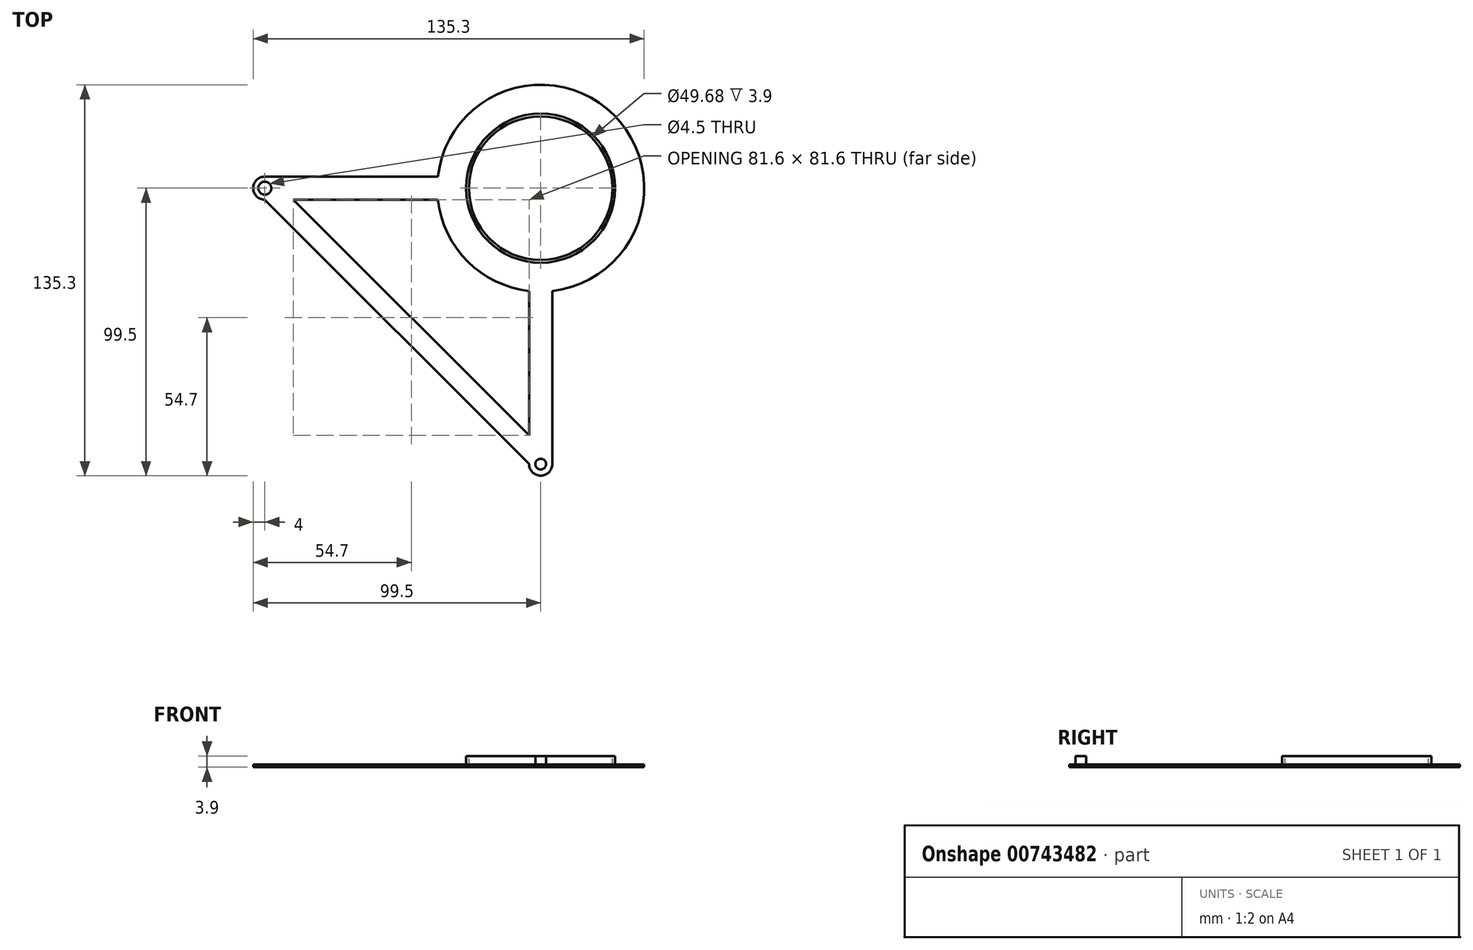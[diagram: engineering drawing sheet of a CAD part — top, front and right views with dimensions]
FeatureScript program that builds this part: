
annotation { "Feature Type Name" : "Feature", "Feature Type Description" : "" }
export const myFeature = defineFeature(function(context is Context, id is Id, definition is map)
    precondition{}
    {
        {
            var Q0;
            Q0=qCreatedBy(makeId("Top.planeOp"),FACE);
            var sketch = newSketch(context, id + "F0", { "sketchPlane" : qUnion([Q0])});
            skCircle(sketch, "E0", {"center": v(-95.5, 0) * mm, "radius": 2.25 * mm});
            skCircle(sketch, "E1", {"center": v(0, -95.5) * mm, "radius": 1.85 * mm});
            skCircle(sketch, "E2", {"center": v(0, 0) * mm, "radius": 24.84 * mm});
            skCircle(sketch, "E3", {"center": v(0, 0) * mm, "radius": 25.8 * mm});
            skCircle(sketch, "E4", {"center": v(0, 0) * mm, "radius": 35.8 * mm});
            skLineSegment(sketch, "E5.bottom", {"start": v(0, 4) * mm, "end": v(-95.5, 4) * mm});
            skLineSegment(sketch, "E5.top", {"start": v(0, -4) * mm, "end": v(-95.5, -4) * mm});
            skLineSegment(sketch, "E5.left", {"start": v(0, 4) * mm, "end": v(0, -4) * mm});
            skLineSegment(sketch, "E5.right", {"start": v(-95.5, 4) * mm, "end": v(-95.5, -4) * mm});
            skLineSegment(sketch, "E6.bottom", {"start": v(-4, 0) * mm, "end": v(4, 0) * mm});
            skLineSegment(sketch, "E6.top", {"start": v(-4, -95.5) * mm, "end": v(4, -95.5) * mm});
            skLineSegment(sketch, "E6.left", {"start": v(-4, 0) * mm, "end": v(-4, -95.5) * mm});
            skLineSegment(sketch, "E6.right", {"start": v(4, 0) * mm, "end": v(4, -95.5) * mm});
            skCircle(sketch, "E7", {"center": v(-95.5, 0) * mm, "radius": 4 * mm});
            skCircle(sketch, "E8", {"center": v(0, -95.5) * mm, "radius": 4 * mm});
            skLineSegment(sketch, "E9", {"start": v(-95.5, -4) * mm, "end": v(-4, -95.5) * mm});
            skLineSegment(sketch, "E10", {"start": v(-85.6, -4) * mm, "end": v(-4, -85.6) * mm});
            skSolve(sketch);
        }
        {
            var Q0;
            {var subQ5=sQuery(id+"F0.wireOp",EDGE,"E5.bottom");var subQ7=sQuery(id+"F0.wireOp",EDGE,"E4");var subQ9=makeQuery(id+"F0.imprint","INTERSECT",VERTEX,{"derivedFrom":[subQ7,subQ5]});Q0=makeQuery(id+"F0.imprint","IMPRINT",FACE,{"disambiguationData":[TD([[makeQuery(id+"F0.imprint","IMPRINT",EDGE,{"disambiguationData":[TD([[subQ9,-1.0]])],"derivedFrom":subQ7}),-1.0]])]});}
            var Q1;
            {var subQ0=sQuery(id+"F0.wireOp",EDGE,"E5.right");var subQ1=sQuery(id+"F0.wireOp",EDGE,"E0");var subQ2=makeQuery(id+"F0.imprint","INTERSECT",VERTEX,{"disambiguationData":[OD(0.0)],"derivedFrom":[subQ1,subQ0]});Q1=makeQuery(id+"F0.imprint","IMPRINT",FACE,{"disambiguationData":[TD([[makeQuery(id+"F0.imprint","IMPRINT",EDGE,{"disambiguationData":[TD([[subQ2,1.0]])],"derivedFrom":subQ1}),-1.0]])]});}
            var Q2;
            {var subQ0=sQuery(id+"F0.wireOp",EDGE,"E5.right");var subQ1=sQuery(id+"F0.wireOp",EDGE,"E0");var subQ2=makeQuery(id+"F0.imprint","INTERSECT",VERTEX,{"disambiguationData":[OD(0.0)],"derivedFrom":[subQ1,subQ0]});Q2=makeQuery(id+"F0.imprint","IMPRINT",FACE,{"disambiguationData":[TD([[makeQuery(id+"F0.imprint","IMPRINT",EDGE,{"disambiguationData":[TD([[subQ2,-1.0]])],"derivedFrom":subQ1}),-1.0]])]});}
            var Q3;
            {var subQ0=sQuery(id+"F0.wireOp",EDGE,"E9");Q3=makeQuery(id+"F0.imprint","IMPRINT",FACE,{"disambiguationData":[TD([[makeQuery(id+"F0.imprint","IMPRINT",EDGE,{"derivedFrom":subQ0}),1.0]])]});}
            var Q4;
            {var subQ0=sQuery(id+"F0.wireOp",EDGE,"E6.top");var subQ1=sQuery(id+"F0.wireOp",EDGE,"E1");var subQ2=makeQuery(id+"F0.imprint","INTERSECT",VERTEX,{"disambiguationData":[OD(0.0)],"derivedFrom":[subQ1,subQ0]});Q4=makeQuery(id+"F0.imprint","IMPRINT",FACE,{"disambiguationData":[TD([[makeQuery(id+"F0.imprint","IMPRINT",EDGE,{"disambiguationData":[TD([[subQ2,1.0]])],"derivedFrom":subQ1}),-1.0]])]});}
            var Q5;
            {var subQ0=sQuery(id+"F0.wireOp",EDGE,"E6.top");var subQ1=sQuery(id+"F0.wireOp",EDGE,"E1");var subQ2=makeQuery(id+"F0.imprint","INTERSECT",VERTEX,{"disambiguationData":[OD(0.0)],"derivedFrom":[subQ1,subQ0]});Q5=makeQuery(id+"F0.imprint","IMPRINT",FACE,{"disambiguationData":[TD([[makeQuery(id+"F0.imprint","IMPRINT",EDGE,{"disambiguationData":[TD([[subQ2,-1.0]])],"derivedFrom":subQ1}),-1.0]])]});}
            var Q6;
            {var subQ0=sQuery(id+"F0.wireOp",EDGE,"E6.top");var subQ1=sQuery(id+"F0.wireOp",EDGE,"E1");var subQ2=makeQuery(id+"F0.imprint","INTERSECT",VERTEX,{"disambiguationData":[OD(0.0)],"derivedFrom":[subQ1,subQ0]});Q6=makeQuery(id+"F0.imprint","IMPRINT",FACE,{"disambiguationData":[TD([[makeQuery(id+"F0.imprint","IMPRINT",EDGE,{"disambiguationData":[TD([[subQ2,1.0]])],"derivedFrom":subQ1}),1.0]])]});}
            var Q7;
            {var subQ0=sQuery(id+"F0.wireOp",EDGE,"E6.top");var subQ1=sQuery(id+"F0.wireOp",EDGE,"E1");var subQ2=makeQuery(id+"F0.imprint","INTERSECT",VERTEX,{"disambiguationData":[OD(0.0)],"derivedFrom":[subQ1,subQ0]});Q7=makeQuery(id+"F0.imprint","IMPRINT",FACE,{"disambiguationData":[TD([[makeQuery(id+"F0.imprint","IMPRINT",EDGE,{"disambiguationData":[TD([[subQ2,-1.0]])],"derivedFrom":subQ1}),1.0]])]});}
            var Q8;
            {var subQ5=sQuery(id+"F0.wireOp",EDGE,"E6.right");var subQ7=sQuery(id+"F0.wireOp",EDGE,"E4");var subQ8=makeQuery(id+"F0.imprint","INTERSECT",VERTEX,{"derivedFrom":[subQ7,subQ5]});Q8=makeQuery(id+"F0.imprint","IMPRINT",FACE,{"disambiguationData":[TD([[makeQuery(id+"F0.imprint","IMPRINT",EDGE,{"disambiguationData":[TD([[subQ8,1.0]])],"derivedFrom":subQ7}),-1.0]])]});}
            var Q9;
            {var subQ0=sQuery(id+"F0.wireOp",EDGE,"E5.top");var subQ1=sQuery(id+"F0.wireOp",EDGE,"E3");var subQ2=makeQuery(id+"F0.imprint","INTERSECT",VERTEX,{"derivedFrom":[subQ1,subQ0]});Q9=makeQuery(id+"F0.imprint","IMPRINT",FACE,{"disambiguationData":[TD([[makeQuery(id+"F0.imprint","IMPRINT",EDGE,{"disambiguationData":[TD([[subQ2,-1.0]])],"derivedFrom":subQ1}),-1.0]])]});}
            var Q10;
            {var subQ0=sQuery(id+"F0.wireOp",EDGE,"E5.top");var subQ1=sQuery(id+"F0.wireOp",EDGE,"E3");var subQ2=makeQuery(id+"F0.imprint","INTERSECT",VERTEX,{"derivedFrom":[subQ1,subQ0]});Q10=makeQuery(id+"F0.imprint","IMPRINT",FACE,{"disambiguationData":[TD([[makeQuery(id+"F0.imprint","IMPRINT",EDGE,{"disambiguationData":[TD([[subQ2,1.0]])],"derivedFrom":subQ1}),-1.0]])]});}
            var Q11;
            {var subQ0=sQuery(id+"F0.wireOp",EDGE,"E5.bottom");var subQ1=sQuery(id+"F0.wireOp",EDGE,"E3");var subQ2=makeQuery(id+"F0.imprint","INTERSECT",VERTEX,{"derivedFrom":[subQ1,subQ0]});Q11=makeQuery(id+"F0.imprint","IMPRINT",FACE,{"disambiguationData":[TD([[makeQuery(id+"F0.imprint","IMPRINT",EDGE,{"disambiguationData":[TD([[subQ2,1.0]])],"derivedFrom":subQ1}),-1.0]])]});}
            var Q12;
            {var subQ0=sQuery(id+"F0.wireOp",EDGE,"E6.left");var subQ1=sQuery(id+"F0.wireOp",EDGE,"E3");var subQ2=makeQuery(id+"F0.imprint","INTERSECT",VERTEX,{"derivedFrom":[subQ1,subQ0]});Q12=makeQuery(id+"F0.imprint","IMPRINT",FACE,{"disambiguationData":[TD([[makeQuery(id+"F0.imprint","IMPRINT",EDGE,{"disambiguationData":[TD([[subQ2,-1.0]])],"derivedFrom":subQ1}),-1.0]])]});}
            var Q13;
            {var subQ0=sQuery(id+"F0.wireOp",EDGE,"E5.top");var subQ1=sQuery(id+"F0.wireOp",EDGE,"E2");var subQ2=makeQuery(id+"F0.imprint","INTERSECT",VERTEX,{"derivedFrom":[subQ1,subQ0]});Q13=makeQuery(id+"F0.imprint","IMPRINT",FACE,{"disambiguationData":[TD([[makeQuery(id+"F0.imprint","IMPRINT",EDGE,{"disambiguationData":[TD([[subQ2,-1.0]])],"derivedFrom":subQ1}),-1.0]])]});}
            var Q14;
            {var subQ0=sQuery(id+"F0.wireOp",EDGE,"E5.top");var subQ1=sQuery(id+"F0.wireOp",EDGE,"E2");var subQ2=makeQuery(id+"F0.imprint","INTERSECT",VERTEX,{"derivedFrom":[subQ1,subQ0]});Q14=makeQuery(id+"F0.imprint","IMPRINT",FACE,{"disambiguationData":[TD([[makeQuery(id+"F0.imprint","IMPRINT",EDGE,{"disambiguationData":[TD([[subQ2,1.0]])],"derivedFrom":subQ1}),-1.0]])]});}
            var Q15;
            {var subQ0=sQuery(id+"F0.wireOp",EDGE,"E5.bottom");var subQ1=sQuery(id+"F0.wireOp",EDGE,"E2");var subQ2=makeQuery(id+"F0.imprint","INTERSECT",VERTEX,{"derivedFrom":[subQ1,subQ0]});Q15=makeQuery(id+"F0.imprint","IMPRINT",FACE,{"disambiguationData":[TD([[makeQuery(id+"F0.imprint","IMPRINT",EDGE,{"disambiguationData":[TD([[subQ2,1.0]])],"derivedFrom":subQ1}),-1.0]])]});}
            var Q16;
            {var subQ0=sQuery(id+"F0.wireOp",EDGE,"E6.left");var subQ1=sQuery(id+"F0.wireOp",EDGE,"E2");var subQ2=makeQuery(id+"F0.imprint","INTERSECT",VERTEX,{"derivedFrom":[subQ1,subQ0]});Q16=makeQuery(id+"F0.imprint","IMPRINT",FACE,{"disambiguationData":[TD([[makeQuery(id+"F0.imprint","IMPRINT",EDGE,{"disambiguationData":[TD([[subQ2,-1.0]])],"derivedFrom":subQ1}),-1.0]])]});}
            extrude(context, id + "F1", {"entities" : qUnion([Q0, Q1, Q2, Q3, Q4, Q5, Q6, Q7, Q8, Q9, Q10, Q11, Q12, Q13, Q14, Q15, Q16]), "oppositeDirection" : true, "depth" : 0.9 * mm, "offsetDistance" : 25 * mm});
        }
        {
            var Q0;
            {var subQ0=sQuery(id+"F0.wireOp",EDGE,"E5.bottom");var subQ1=sQuery(id+"F0.wireOp",EDGE,"E2");var subQ2=makeQuery(id+"F0.imprint","INTERSECT",VERTEX,{"derivedFrom":[subQ1,subQ0]});Q0=makeQuery(id+"F0.imprint","IMPRINT",FACE,{"disambiguationData":[TD([[makeQuery(id+"F0.imprint","IMPRINT",EDGE,{"disambiguationData":[TD([[subQ2,1.0]])],"derivedFrom":subQ1}),-1.0]])]});}
            var Q1;
            {var subQ0=sQuery(id+"F0.wireOp",EDGE,"E5.top");var subQ1=sQuery(id+"F0.wireOp",EDGE,"E2");var subQ2=makeQuery(id+"F0.imprint","INTERSECT",VERTEX,{"derivedFrom":[subQ1,subQ0]});Q1=makeQuery(id+"F0.imprint","IMPRINT",FACE,{"disambiguationData":[TD([[makeQuery(id+"F0.imprint","IMPRINT",EDGE,{"disambiguationData":[TD([[subQ2,1.0]])],"derivedFrom":subQ1}),-1.0]])]});}
            var Q2;
            {var subQ0=sQuery(id+"F0.wireOp",EDGE,"E5.top");var subQ1=sQuery(id+"F0.wireOp",EDGE,"E2");var subQ2=makeQuery(id+"F0.imprint","INTERSECT",VERTEX,{"derivedFrom":[subQ1,subQ0]});Q2=makeQuery(id+"F0.imprint","IMPRINT",FACE,{"disambiguationData":[TD([[makeQuery(id+"F0.imprint","IMPRINT",EDGE,{"disambiguationData":[TD([[subQ2,-1.0]])],"derivedFrom":subQ1}),-1.0]])]});}
            var Q3;
            {var subQ0=sQuery(id+"F0.wireOp",EDGE,"E6.left");var subQ1=sQuery(id+"F0.wireOp",EDGE,"E2");var subQ2=makeQuery(id+"F0.imprint","INTERSECT",VERTEX,{"derivedFrom":[subQ1,subQ0]});Q3=makeQuery(id+"F0.imprint","IMPRINT",FACE,{"disambiguationData":[TD([[makeQuery(id+"F0.imprint","IMPRINT",EDGE,{"disambiguationData":[TD([[subQ2,-1.0]])],"derivedFrom":subQ1}),-1.0]])]});}
            extrude(context, id + "F2", {"entities" : qUnion([Q0, Q1, Q2, Q3]), "operationType" : NewBodyOperationType.ADD, "depth" : 3 * mm, "offsetDistance" : 25 * mm});
        }
        {
            var Q0;
            {var subQ0=sQuery(id+"F0.wireOp",EDGE,"E6.top");var subQ1=sQuery(id+"F0.wireOp",EDGE,"E1");var subQ2=makeQuery(id+"F0.imprint","INTERSECT",VERTEX,{"disambiguationData":[OD(0.0)],"derivedFrom":[subQ1,subQ0]});Q0=makeQuery(id+"F0.imprint","IMPRINT",FACE,{"disambiguationData":[TD([[makeQuery(id+"F0.imprint","IMPRINT",EDGE,{"disambiguationData":[TD([[subQ2,-1.0]])],"derivedFrom":subQ1}),1.0]])]});}
            var Q1;
            {var subQ0=sQuery(id+"F0.wireOp",EDGE,"E6.top");var subQ1=sQuery(id+"F0.wireOp",EDGE,"E1");var subQ2=makeQuery(id+"F0.imprint","INTERSECT",VERTEX,{"disambiguationData":[OD(0.0)],"derivedFrom":[subQ1,subQ0]});Q1=makeQuery(id+"F0.imprint","IMPRINT",FACE,{"disambiguationData":[TD([[makeQuery(id+"F0.imprint","IMPRINT",EDGE,{"disambiguationData":[TD([[subQ2,1.0]])],"derivedFrom":subQ1}),1.0]])]});}
            extrude(context, id + "F3", {"entities" : qUnion([Q0, Q1]), "operationType" : NewBodyOperationType.ADD, "depth" : 3 * mm, "offsetDistance" : 25 * mm});
        }
    });
